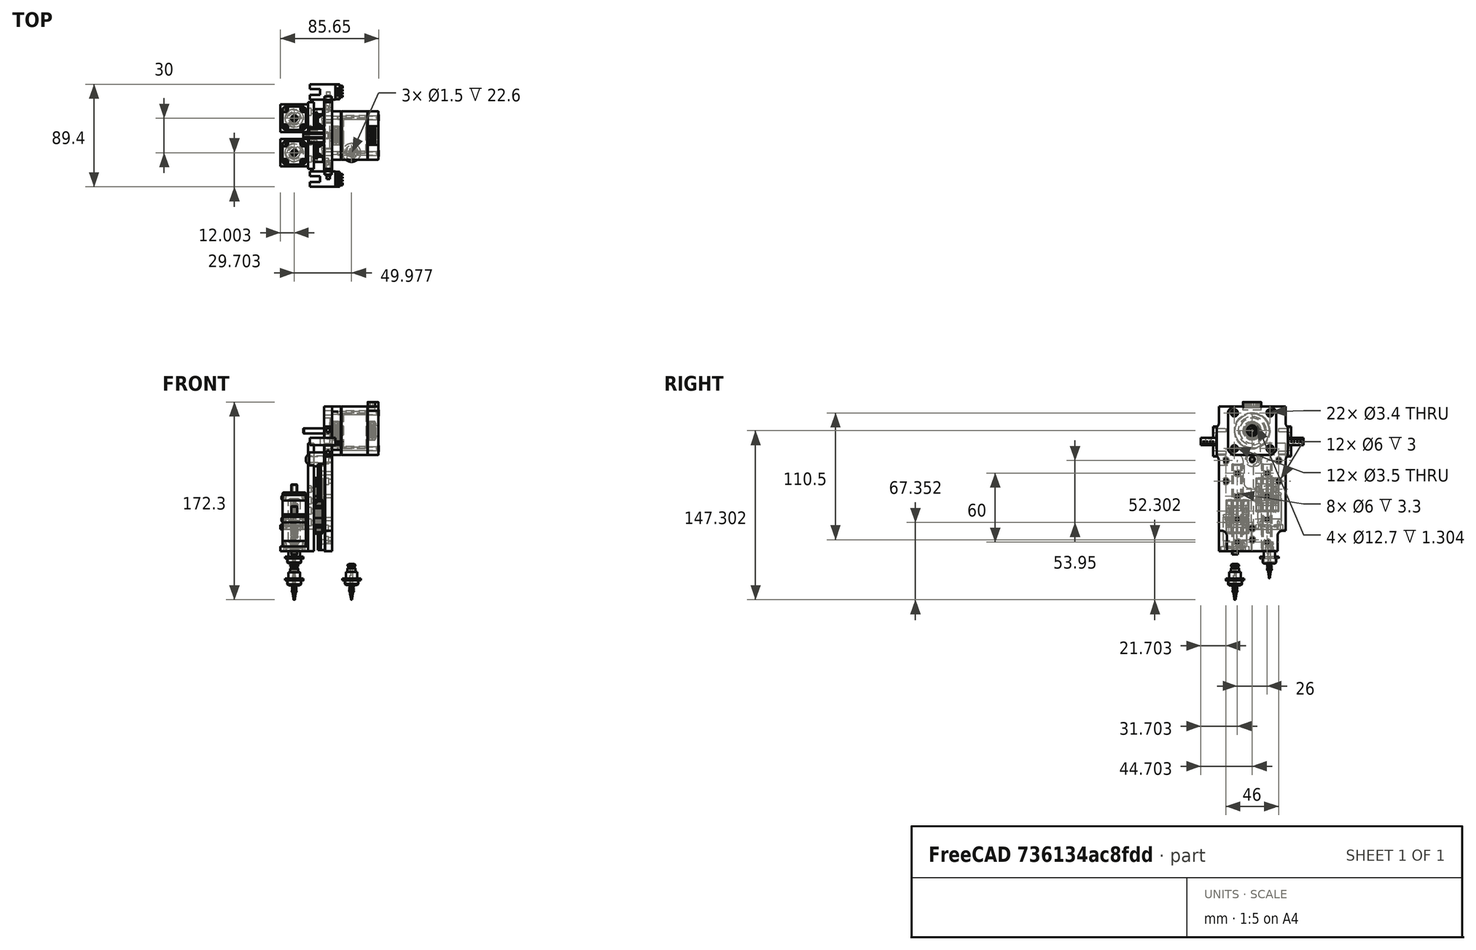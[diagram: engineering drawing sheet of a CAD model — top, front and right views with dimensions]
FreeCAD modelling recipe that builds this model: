
FCSTD DOCUMENT  (FreeCAD 0.19R22262 (Git))
Label: ToolChangerSmallSketch
License: All rights reserved
LicenseURL: http://en.wikipedia.org/wiki/All_rights_reserved
objects: Part::FeaturePython×3
note: 2 computed .brp shape members not serialized (recipe doc carries the construction recipe); baked Part::Feature solids carry a one-line shape summary decoded from their .brp

FEATURE [Part::FeaturePython] b_Juki_503_001_  label="Juki-503_001"  # a2plus imported part (geometry in sourceFile) (typed FeaturePython)
  a2p_Version = V0.1
  fixedPosition = true
  sourceFile = ./../Model/Juki-503.fcstd
  sourcePart = Juki-503
  subassemblyImport = false
  timeLastImport = 1.56076e+09
  updateColors = true
FEATURE [Part::FeaturePython] b_SMT_HeadDual_001_  label="SMT_HeadDual_001"  # a2plus imported part (geometry in sourceFile) (typed FeaturePython)
  Placement = pos=(-3.9773,14.9832,168.112) rot=(0,1,0;4.71239rad)
  a2p_Version = V0.1
  fixedPosition = false
  sourceFile = ./SMT_HeadDual.FCStd
  subassemblyImport = true
  timeLastImport = 1.56232e+09
  updateColors = true
FEATURE [Part::FeaturePython] Array  # Draft array (typed FeaturePython)
  Angle = 360
  ArrayType = 1
  Axis = (0,0,1)
  Base = -> b_Juki_503_001_
  Center = (-1,0,0)
  Count = 8
  ExpandArray = false
  Fuse = false
  IntervalAxis = (0,0,0)
  IntervalX = (50,0,0)
  IntervalY = (0,50,0)
  IntervalZ = (0,0,50)
  NumberCircles = 3
  NumberPolar = 8
  NumberX = 2
  NumberY = 2
  NumberZ = 1
  PlacementList = 8 placements: [(0,0,0),(-0.292893,0.707107,0),(-1,1,0),(-1.70711,0.707107,0),(-2,1.22465e-16,0),(-1.70711,-0.707107,0),(-1,-1,0),(-0.292893,-0.707107,0)]
  RadialDistance = 50
  ScaleList = (8) [(1,1,1),(1,1,1),(1,1,1),(1,1,1),(1,1,1),(1,1,1),(1,1,1),(1,1,1)]
  Symmetry = 1
  TangentialDistance = 25
